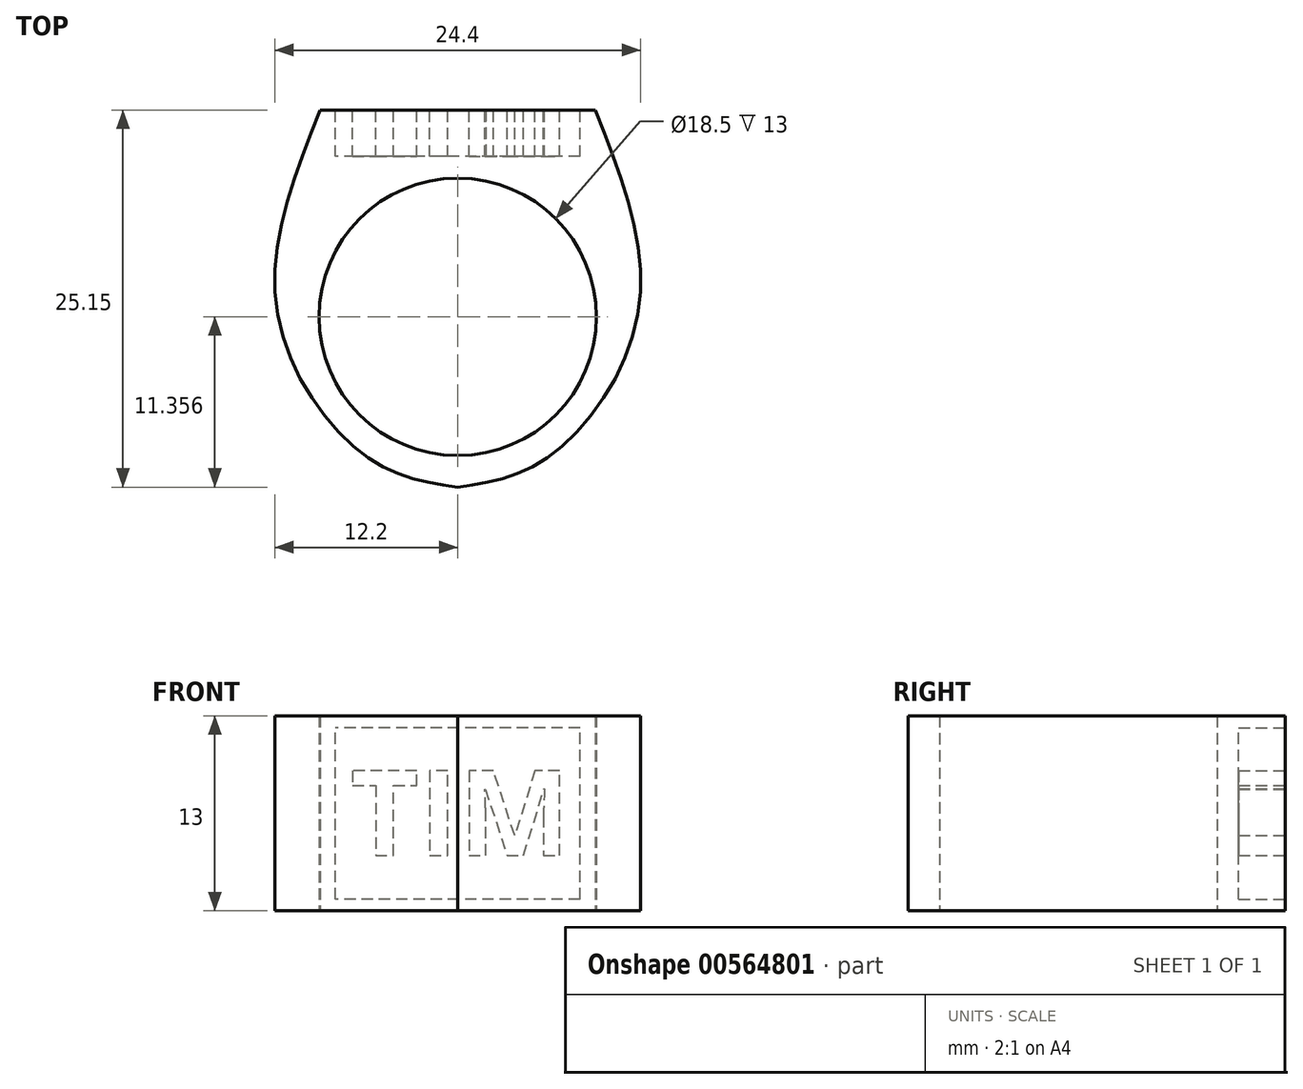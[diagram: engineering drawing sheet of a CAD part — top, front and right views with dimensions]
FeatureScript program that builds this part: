
annotation { "Feature Type Name" : "Feature", "Feature Type Description" : "" }
export const myFeature = defineFeature(function(context is Context, id is Id, definition is map)
    precondition{}
    {
        {
            var Q0;
            Q0=qCreatedBy(makeId("Top.planeOp"),FACE);
            var sketch = newSketch(context, id + "F0", { "sketchPlane" : qUnion([Q0])});
            skCircle(sketch, "E0", {"center": v(0, -0.32) * mm, "radius": 9.25 * mm});
            skLineSegment(sketch, "E1", {"start": v(0, 0) * mm, "end": v(0, -9.57) * mm});
            skLineSegment(sketch, "E2", {"start": v(0, -9.57) * mm, "end": v(0, -11.68) * mm});
            skFitSpline(sketch, "E3", {"points": [v(0, -11.68) * mm, v(-5.98, -9.72) * mm, v(-12.04, 0) * mm, v(-9.19, 13.47) * mm], "startDerivative": vector(-22.84, 3.33) * mm, "endDerivative": vector(13.83, 35.28) * mm});
            skLineSegment(sketch, "E4", {"start": v(-9.19, 13.47) * mm, "end": v(0, 13.47) * mm});
            skLineSegment(sketch, "E5", {"start": v(0, 13.47) * mm, "end": v(0, -11.68) * mm});
            skFitSpline(sketch, "E6.MirrorCS", {"points": [v(0, -11.68) * mm, v(5.98, -9.72) * mm, v(12.04, 0) * mm, v(9.19, 13.47) * mm], "startDerivative": vector(22.84, 3.33) * mm, "endDerivative": vector(-13.83, 35.28) * mm});
            skLineSegment(sketch, "E7.MirrorCS", {"start": v(9.19, 13.47) * mm, "end": v(0, 13.47) * mm});
            skSolve(sketch);
        }
        {
            var Q0;
            {var subQ4=sQuery(id+"F0.wireOp",EDGE,"E3");Q0=makeQuery(id+"F0.imprint","IMPRINT",FACE,{"disambiguationData":[TD([[makeQuery(id+"F0.imprint","IMPRINT",EDGE,{"derivedFrom":subQ4}),-1.0]])]});}
            var Q1;
            {var subQ0=sQuery(id+"F0.wireOp",EDGE,"E6.MirrorCS");Q1=makeQuery(id+"F0.imprint","IMPRINT",FACE,{"disambiguationData":[TD([[makeQuery(id+"F0.imprint","IMPRINT",EDGE,{"derivedFrom":subQ0}),1.0]])]});}
            extrude(context, id + "F1", {"entities" : qUnion([Q0, Q1]), "depth" : 13 * mm, "offsetDistance" : 25 * mm});
        }
        {
            var Q0;
            Q0=makeQuery(id+"F1.opExtrude","SWEPT_FACE",FACE,{"disambiguationData":[OSD([sQuery(id+"F0.wireOp",EDGE,"E4"),sQuery(id+"F0.wireOp",EDGE,"E7.MirrorCS")])]});
            var sketch = newSketch(context, id + "F2", { "sketchPlane" : qUnion([Q0])});
            skLineSegment(sketch, "E8", {"start": v(-9.19, 6.5) * mm, "end": v(9.19, 6.5) * mm});
            skLineSegment(sketch, "E9", {"start": v(9.19, 6.5) * mm, "end": v(0, 13) * mm});
            skLineSegment(sketch, "E10", {"start": v(0, 13) * mm, "end": v(0, 0) * mm});
            skLineSegment(sketch, "E11.bottom", {"start": v(-8.15, 0.79) * mm, "end": v(8.15, 0.79) * mm});
            skLineSegment(sketch, "E11.top", {"start": v(-8.15, 12.21) * mm, "end": v(8.15, 12.21) * mm});
            skLineSegment(sketch, "E11.left", {"start": v(-8.15, 0.79) * mm, "end": v(-8.15, 12.21) * mm});
            skLineSegment(sketch, "E11.right", {"start": v(8.15, 0.79) * mm, "end": v(8.15, 12.21) * mm});
            skPoint(sketch, "E11.middle", {"position": v(0, 6.5) * mm});
            skSolve(sketch);
        }
        {
            var Q0;
            Q0=makeQuery(id+"F1.opExtrude","SWEPT_FACE",FACE,{"disambiguationData":[OSD([sQuery(id+"F0.wireOp",EDGE,"E4"),sQuery(id+"F0.wireOp",EDGE,"E7.MirrorCS")])]});
            var sketch = newSketch(context, id + "F3", { "sketchPlane" : qUnion([Q0])});
            skLineSegment(sketch, "E12", {"start": v(0, 11.09) * mm, "end": v(0, 4.76) * mm});
            skPoint(sketch, "E12.startSnap0", {"position": v(0, 12.21) * mm});
            skLineSegment(sketch, "E13", {"start": v(0, 4.76) * mm, "end": v(5.4, 4.76) * mm});
            skFitSpline(sketch, "E14", {"points": [v(5.4, 4.76) * mm, v(4.98, 5.08) * mm, v(2.47, 5.08) * mm, v(0, 5.29) * mm], "startDerivative": vector(-4.58, 2.1) * mm, "endDerivative": vector(-6.7, 0.87) * mm});
            skFitSpline(sketch, "E15", {"points": [v(0, 6.07) * mm, v(1.27, 6.95) * mm, v(1.38, 7.7) * mm, v(0, 7.16) * mm], "startDerivative": vector(5.62, 1.4) * mm, "endDerivative": vector(-6.84, -2.99) * mm});
            skFitSpline(sketch, "E16", {"points": [v(0, 11.09) * mm, v(1.45, 11.73) * mm, v(3.85, 10.67) * mm, v(2.58, 8.61) * mm, v(1.38, 7.7) * mm], "startDerivative": vector(5.24, 4.13) * mm, "endDerivative": vector(-4.9, -3.34) * mm});
            skCircle(sketch, "E17", {"center": v(1.27, 9.5) * mm, "radius": 0.87 * mm});
            skCircle(sketch, "E18", {"center": v(1.27, 9.5) * mm, "radius": 0.47 * mm});
            skFitSpline(sketch, "E19", {"points": [v(5.4, 4.76) * mm, v(4.49, 4.47) * mm, v(2.5, 4.58) * mm, v(0, 4.47) * mm], "startDerivative": vector(-3.35, -1.5) * mm, "endDerivative": vector(-6.31, -0.54) * mm});
            skLineSegment(sketch, "E20", {"start": v(0, 4.76) * mm, "end": v(0, 4.47) * mm});
            skFitSpline(sketch, "E21.MirrorCS", {"points": [v(0, 6.07) * mm, v(-1.27, 6.95) * mm, v(-1.38, 7.7) * mm, v(0, 7.16) * mm], "startDerivative": vector(-5.62, 1.4) * mm, "endDerivative": vector(6.84, -2.99) * mm});
            skFitSpline(sketch, "E22.MirrorCS", {"points": [v(0, 11.09) * mm, v(-1.45, 11.73) * mm, v(-3.85, 10.67) * mm, v(-2.58, 8.61) * mm, v(-1.38, 7.7) * mm], "startDerivative": vector(-5.24, 4.13) * mm, "endDerivative": vector(4.9, -3.34) * mm});
            skCircle(sketch, "E23.MirrorC", {"center": v(-1.27, 9.5) * mm, "radius": 0.87 * mm});
            skCircle(sketch, "E24.MirrorC", {"center": v(-1.27, 9.5) * mm, "radius": 0.47 * mm});
            skFitSpline(sketch, "E25.MirrorCS", {"points": [v(-5.4, 4.76) * mm, v(-4.98, 5.08) * mm, v(-2.47, 5.08) * mm, v(0, 5.29) * mm], "startDerivative": vector(4.58, 2.1) * mm, "endDerivative": vector(6.7, 0.87) * mm});
            skLineSegment(sketch, "E26.MirrorCS", {"start": v(0, 4.76) * mm, "end": v(-5.4, 4.76) * mm});
            skFitSpline(sketch, "E27.MirrorCS", {"points": [v(-5.4, 4.76) * mm, v(-4.49, 4.47) * mm, v(-2.5, 4.58) * mm, v(0, 4.47) * mm], "startDerivative": vector(3.35, -1.5) * mm, "endDerivative": vector(6.31, -0.54) * mm});
            skSolve(sketch);
        }
        {
            var Q0;
            Q0=makeQuery(id+"F3.imprint","IMPRINT",FACE,{"disambiguationData":[TD([[makeQuery(id+"F3.imprint","IMPRINT",EDGE,{"derivedFrom":sQuery(id+"F3.wireOp",EDGE,"E14")}),-1.0]])]});
            var sketch = newSketch(context, id + "F4", { "sketchPlane" : qUnion([Q0])});
            skText(sketch, "E28", { "text": "MIT\n", "fontName": "OpenSans-Bold.ttf"});
            const initialGuessF4  = {"E28": [-0.0075, 0.0037, 1, 0, 0.0057]};
            skSetInitialGuess(sketch, initialGuessF4);
            skSolve(sketch);
        }
        {
            var Q0;
            Q0=makeQuery(id+"F4.imprint","IMPRINT",FACE,{"disambiguationData":[TD([[makeQuery(id+"F4.imprint","IMPRINT",EDGE,{"derivedFrom":sQuery(id+"F4.wireOp",EDGE,"E28.sketch_text.stroke-19")}),-1.0]])]});
            var Q1;
            Q1=makeQuery(id+"F4.imprint","IMPRINT",FACE,{"disambiguationData":[TD([[makeQuery(id+"F4.imprint","IMPRINT",EDGE,{"derivedFrom":sQuery(id+"F4.wireOp",EDGE,"E28.sketch_text.stroke-0")}),-1.0]])]});
            var Q2;
            Q2=makeQuery(id+"F4.imprint","IMPRINT",FACE,{"disambiguationData":[TD([[makeQuery(id+"F4.imprint","IMPRINT",EDGE,{"derivedFrom":sQuery(id+"F4.wireOp",EDGE,"E28.sketch_text.stroke-23")}),-1.0]])]});
            extrude(context, id + "F5", {"entities" : qUnion([Q0, Q1, Q2]), "operationType" : NewBodyOperationType.ADD, "oppositeDirection" : true, "depth" : 3.76 * mm, "offsetDistance" : 25 * mm});
        }
        {
            var Q0;
            Q0 = qSketchRegion(id + "F4", true);
            var Q1;
            {var subQ0=sQuery(id+"F2.wireOp",EDGE,"E11.left");var subQ1=sQuery(id+"F2.wireOp",EDGE,"E8");var subQ2=makeQuery(id+"F2.imprint","INTERSECT",VERTEX,{"derivedFrom":[subQ1,subQ0]});Q1=makeQuery(id+"F2.imprint","IMPRINT",FACE,{"disambiguationData":[TD([[makeQuery(id+"F2.imprint","IMPRINT",EDGE,{"disambiguationData":[TD([[subQ2,-1.0]])],"derivedFrom":subQ1}),1.0]])]});}
            var Q2;
            {var subQ0=sQuery(id+"F2.wireOp",EDGE,"E11.right");var subQ1=sQuery(id+"F2.wireOp",EDGE,"E9");var subQ2=makeQuery(id+"F2.imprint","INTERSECT",VERTEX,{"derivedFrom":[subQ1,subQ0]});Q2=makeQuery(id+"F2.imprint","IMPRINT",FACE,{"disambiguationData":[TD([[makeQuery(id+"F2.imprint","IMPRINT",EDGE,{"disambiguationData":[TD([[subQ2,-1.0]])],"derivedFrom":subQ1}),-1.0]])]});}
            var Q3;
            {var subQ3=sQuery(id+"F2.wireOp",EDGE,"E10");var subQ5=sQuery(id+"F2.wireOp",EDGE,"E8");var subQ6=makeQuery(id+"F2.imprint","INTERSECT",VERTEX,{"derivedFrom":[subQ5,subQ3]});Q3=makeQuery(id+"F2.imprint","IMPRINT",FACE,{"disambiguationData":[TD([[makeQuery(id+"F2.imprint","IMPRINT",EDGE,{"disambiguationData":[TD([[subQ6,-1.0]])],"derivedFrom":subQ5}),1.0]])]});}
            var Q4;
            {var subQ0=sQuery(id+"F2.wireOp",EDGE,"E10");var subQ1=sQuery(id+"F2.wireOp",EDGE,"E8");var subQ2=makeQuery(id+"F2.imprint","INTERSECT",VERTEX,{"derivedFrom":[subQ1,subQ0]});Q4=makeQuery(id+"F2.imprint","IMPRINT",FACE,{"disambiguationData":[TD([[makeQuery(id+"F2.imprint","IMPRINT",EDGE,{"disambiguationData":[TD([[subQ2,-1.0]])],"derivedFrom":subQ1}),-1.0]])]});}
            var Q5;
            {var subQ0=sQuery(id+"F2.wireOp",EDGE,"E11.left");var subQ1=sQuery(id+"F2.wireOp",EDGE,"E8");var subQ2=makeQuery(id+"F2.imprint","INTERSECT",VERTEX,{"derivedFrom":[subQ1,subQ0]});Q5=makeQuery(id+"F2.imprint","IMPRINT",FACE,{"disambiguationData":[TD([[makeQuery(id+"F2.imprint","IMPRINT",EDGE,{"disambiguationData":[TD([[subQ2,-1.0]])],"derivedFrom":subQ1}),-1.0]])]});}
            extrude(context, id + "F6", {"entities" : qUnion([Q0, Q1, Q2, Q3, Q4, Q5]), "operationType" : NewBodyOperationType.REMOVE, "oppositeDirection" : true, "depth" : 3.1 * mm, "offsetDistance" : 25 * mm});
        }
        {
            var Q0;
            Q0 = qSketchRegion(id + "F4", true);
            extrude(context, id + "F7", {"entities" : qUnion([Q0]), "operationType" : NewBodyOperationType.ADD, "oppositeDirection" : true, "depth" : 3.6 * mm, "offsetDistance" : 25 * mm});
        }
    });
